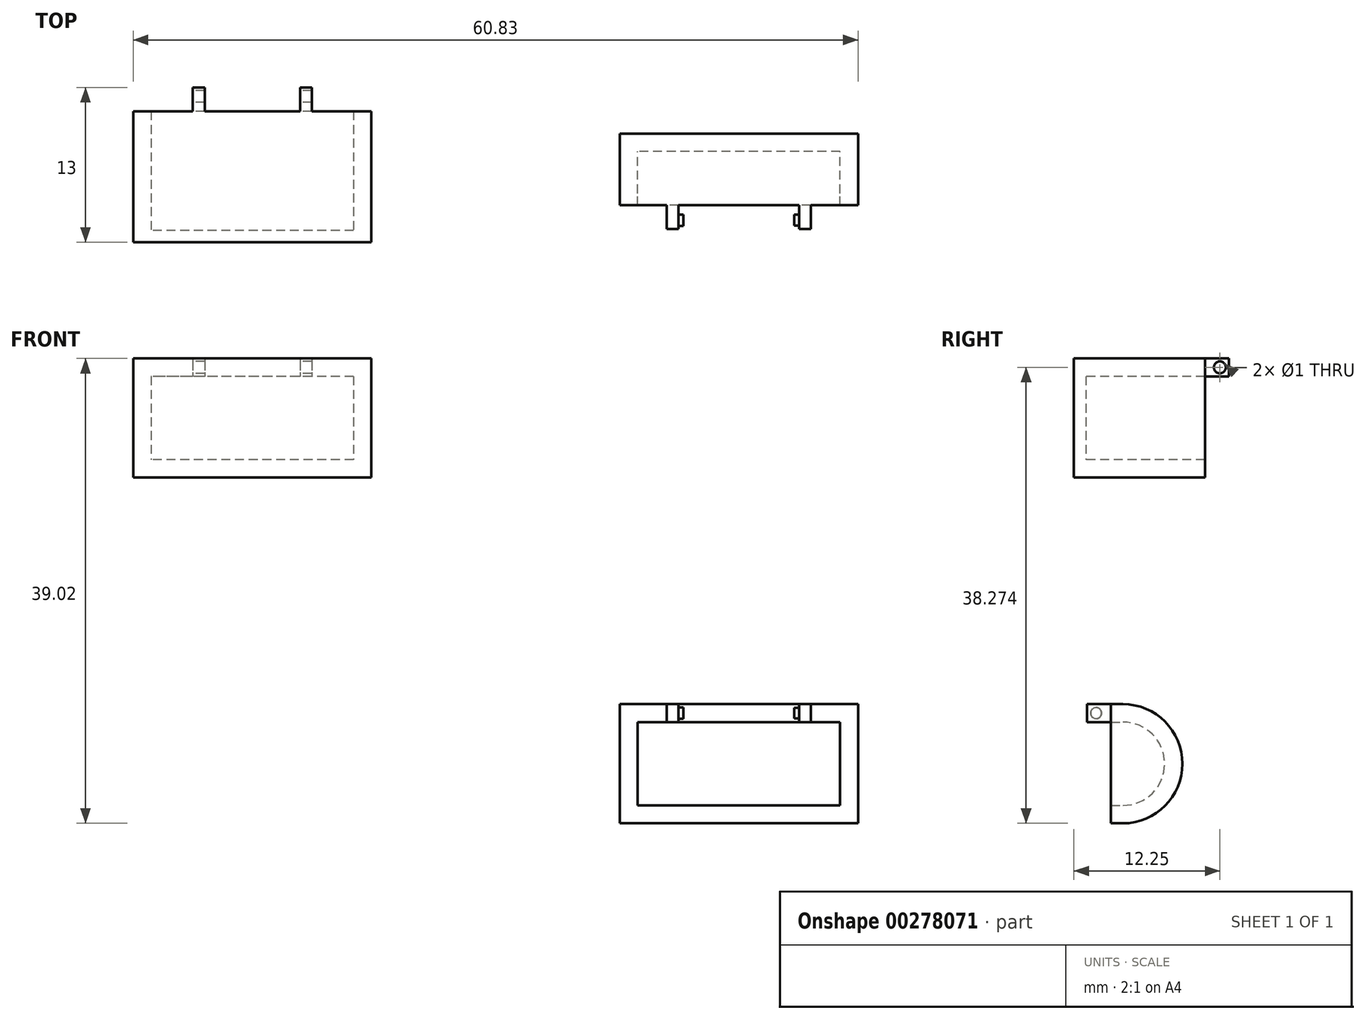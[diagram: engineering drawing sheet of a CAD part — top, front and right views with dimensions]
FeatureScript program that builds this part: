
annotation { "Feature Type Name" : "Feature", "Feature Type Description" : "" }
export const myFeature = defineFeature(function(context is Context, id is Id, definition is map)
    precondition{}
    {
        {
            var Q0;
            Q0=qCreatedBy(makeId("Front.planeOp"),FACE);
            var sketch = newSketch(context, id + "F0", { "sketchPlane" : qUnion([Q0])});
            skLineSegment(sketch, "E0.bottom", {"start": v(-40.83, 8.05) * mm, "end": v(-20.83, 8.05) * mm});
            skLineSegment(sketch, "E0.top", {"start": v(-40.83, -1.95) * mm, "end": v(-20.83, -1.95) * mm});
            skLineSegment(sketch, "E0.left", {"start": v(-40.83, 8.05) * mm, "end": v(-40.83, -1.95) * mm});
            skLineSegment(sketch, "E0.right", {"start": v(-20.83, 8.05) * mm, "end": v(-20.83, -1.95) * mm});
            skSolve(sketch);
        }
        {
            var Q0;
            Q0 = qSketchRegion(id + "F0", true);
            extrude(context, id + "F1", {"entities" : qUnion([Q0]), "oppositeDirection" : true, "depth" : 1 * mm});
        }
        {
            var Q0;
            Q0=makeQuery(id+"F1.opExtrude","CAP_FACE",FACE,{"disambiguationData":[OSD([sQuery(id+"F0.wireOp",EDGE,"E0.bottom"),sQuery(id+"F0.wireOp",EDGE,"E0.top"),sQuery(id+"F0.wireOp",EDGE,"E0.left"),sQuery(id+"F0.wireOp",EDGE,"E0.right")])],"isStart":false});
            var sketch = newSketch(context, id + "F2", { "sketchPlane" : qUnion([Q0])});
            skLineSegment(sketch, "E1.bottom", {"start": v(20.83, 8.05) * mm, "end": v(40.83, 8.05) * mm});
            skLineSegment(sketch, "E1.top", {"start": v(20.83, -1.95) * mm, "end": v(40.83, -1.95) * mm});
            skLineSegment(sketch, "E1.left", {"start": v(20.83, 8.05) * mm, "end": v(20.83, -1.95) * mm});
            skLineSegment(sketch, "E1.right", {"start": v(40.83, 8.05) * mm, "end": v(40.83, -1.95) * mm});
            skLineSegment(sketch, "E2.bottom", {"start": v(22.33, 6.55) * mm, "end": v(39.33, 6.55) * mm});
            skLineSegment(sketch, "E2.top", {"start": v(22.33, -0.45) * mm, "end": v(39.33, -0.45) * mm});
            skLineSegment(sketch, "E2.left", {"start": v(22.33, 6.55) * mm, "end": v(22.33, -0.45) * mm});
            skLineSegment(sketch, "E2.right", {"start": v(39.33, 6.55) * mm, "end": v(39.33, -0.45) * mm});
            skSolve(sketch);
        }
        {
            var Q0;
            Q0 = qSketchRegion(id + "F2", true);
            extrude(context, id + "F3", {"entities" : qUnion([Q0]), "operationType" : NewBodyOperationType.ADD, "depth" : 10 * mm});
        }
        {
            var Q0;
            Q0=makeQuery(id+"F3.opExtrude","CAP_FACE",FACE,{"disambiguationData":[OSD([sQuery(id+"F2.wireOp",EDGE,"E1.bottom"),sQuery(id+"F2.wireOp",EDGE,"E1.top"),sQuery(id+"F2.wireOp",EDGE,"E1.left"),sQuery(id+"F2.wireOp",EDGE,"E1.right"),sQuery(id+"F2.wireOp",EDGE,"E2.bottom"),sQuery(id+"F2.wireOp",EDGE,"E2.top"),sQuery(id+"F2.wireOp",EDGE,"E2.left"),sQuery(id+"F2.wireOp",EDGE,"E2.right")])],"isStart":false});
            var sketch = newSketch(context, id + "F4", { "sketchPlane" : qUnion([Q0])});
            skLineSegment(sketch, "E3.bottom", {"start": v(25.83, 8.05) * mm, "end": v(26.83, 8.05) * mm});
            skLineSegment(sketch, "E3.top", {"start": v(25.83, 6.55) * mm, "end": v(26.83, 6.55) * mm});
            skLineSegment(sketch, "E3.left", {"start": v(25.83, 8.05) * mm, "end": v(25.83, 6.55) * mm});
            skLineSegment(sketch, "E3.right", {"start": v(26.83, 8.05) * mm, "end": v(26.83, 6.55) * mm});
            skLineSegment(sketch, "E4.bottom", {"start": v(34.83, 8.05) * mm, "end": v(35.83, 8.05) * mm});
            skLineSegment(sketch, "E4.top", {"start": v(34.83, 6.55) * mm, "end": v(35.83, 6.55) * mm});
            skLineSegment(sketch, "E4.left", {"start": v(34.83, 8.05) * mm, "end": v(34.83, 6.55) * mm});
            skLineSegment(sketch, "E4.right", {"start": v(35.83, 8.05) * mm, "end": v(35.83, 6.55) * mm});
            skSolve(sketch);
        }
        {
            var Q0;
            Q0 = qSketchRegion(id + "F4", true);
            extrude(context, id + "F5", {"entities" : qUnion([Q0]), "operationType" : NewBodyOperationType.ADD, "depth" : 2 * mm});
        }
        {
            var Q0;
            Q0=makeQuery(id+"F5.opExtrude","SWEPT_FACE",FACE,{"disambiguationData":[OSD([sQuery(id+"F4.wireOp",EDGE,"E4.right")])]});
            var sketch = newSketch(context, id + "F6", { "sketchPlane" : qUnion([Q0])});
            skCircle(sketch, "E5", {"center": v(-12.25, 7.3) * mm, "radius": 0.5 * mm});
            skSolve(sketch);
        }
        {
            var Q0;
            Q0 = qSketchRegion(id + "F6", true);
            extrude(context, id + "F7", {"entities" : qUnion([Q0]), "operationType" : NewBodyOperationType.REMOVE, "oppositeDirection" : true, "depth" : 25 * mm});
        }
        {
            var Q0;
            Q0=qCreatedBy(makeId("Right.planeOp"),FACE);
            var sketch = newSketch(context, id + "F8", { "sketchPlane" : qUnion([Q0])});
            skArc(sketch, "E6", {"start": v(4.12, -30.97) * mm, "mid": v(9.12, -25.97) * mm, "end": v(4.12, -20.97) * mm});
            skLineSegment(sketch, "E7.bottom", {"start": v(4.12, -20.97) * mm, "end": v(3.12, -20.97) * mm});
            skLineSegment(sketch, "E7.top", {"start": v(4.12, -30.97) * mm, "end": v(3.12, -30.97) * mm});
            skLineSegment(sketch, "E7.right", {"start": v(3.12, -20.97) * mm, "end": v(3.12, -30.97) * mm});
            skSolve(sketch);
        }
        {
            var Q0;
            Q0 = qSketchRegion(id + "F8", true);
            extrude(context, id + "F9", {"entities" : qUnion([Q0]), "depth" : 20 * mm});
        }
        {
            var Q0;
            Q0=makeQuery(id+"F9.opExtrude","CAP_FACE",FACE,{"disambiguationData":[OSD([sQuery(id+"F8.wireOp",EDGE,"E6"),sQuery(id+"F8.wireOp",EDGE,"E7.bottom"),sQuery(id+"F8.wireOp",EDGE,"E7.top"),sQuery(id+"F8.wireOp",EDGE,"E7.right")])],"isStart":true});
            cPlane(context, id + "F10", {"entities" : qUnion([Q0]), "cplaneType" : CPlaneType.OFFSET, "offset" : 1.5 * mm, "oppositeDirection" : true, "width" : 150 * mm, "height" : 150 * mm});
        }
        {
            var Q0;
            Q0=qCreatedBy(id+"F10.planeOp",FACE);
            var sketch = newSketch(context, id + "F11", { "sketchPlane" : qUnion([Q0])});
            skArc(sketch, "E8.0", {"start": v(-4.12, -30.97) * mm, "mid": v(-9.12, -25.97) * mm, "end": v(-4.12, -20.97) * mm});
            skLineSegment(sketch, "E9.0", {"start": v(-3.12, -20.97) * mm, "end": v(-3.12, -29.47) * mm});
            skLineSegment(sketch, "E10.0", {"start": v(-4.12, -20.97) * mm, "end": v(-3.12, -20.97) * mm});
            skLineSegment(sketch, "E11.bottom", {"start": v(-3.12, -29.47) * mm, "end": v(-4.12, -29.47) * mm});
            skLineSegment(sketch, "E11.top", {"start": v(-3.12, -22.47) * mm, "end": v(-4.12, -22.47) * mm});
            skLineSegment(sketch, "E11.left", {"start": v(-3.12, -29.47) * mm, "end": v(-3.12, -22.47) * mm});
            skArc(sketch, "E12", {"start": v(-4.12, -22.47) * mm, "mid": v(-7.62, -25.97) * mm, "end": v(-4.12, -29.47) * mm});
            skPoint(sketch, "E13.orphan", {"position": v(-3.12, -30.97) * mm});
            skSolve(sketch);
        }
        {
            var Q0;
            Q0 = qSketchRegion(id + "F11", true);
            extrude(context, id + "F12", {"entities" : qUnion([Q0]), "operationType" : NewBodyOperationType.REMOVE, "oppositeDirection" : true, "depth" : (20 - 2 * 1.5) * mm});
        }
        {
            var Q0;
            Q0=makeQuery(id+"F9.opExtrude","SWEPT_FACE",FACE,{"disambiguationData":[OSD([sQuery(id+"F8.wireOp",EDGE,"E7.right")])]});
            var sketch = newSketch(context, id + "F13", { "sketchPlane" : qUnion([Q0])});
            skLineSegment(sketch, "E14.bottom", {"start": v(3.95, -20.97) * mm, "end": v(4.95, -20.97) * mm});
            skLineSegment(sketch, "E14.top", {"start": v(3.95, -22.47) * mm, "end": v(4.95, -22.47) * mm});
            skLineSegment(sketch, "E14.left", {"start": v(3.95, -20.97) * mm, "end": v(3.95, -22.47) * mm});
            skLineSegment(sketch, "E14.right", {"start": v(4.95, -20.97) * mm, "end": v(4.95, -22.47) * mm});
            skLineSegment(sketch, "E15.bottom", {"start": v(16.05, -20.97) * mm, "end": v(15.05, -20.97) * mm});
            skLineSegment(sketch, "E15.top", {"start": v(16.05, -22.47) * mm, "end": v(15.05, -22.47) * mm});
            skLineSegment(sketch, "E15.left", {"start": v(16.05, -20.97) * mm, "end": v(16.05, -22.47) * mm});
            skLineSegment(sketch, "E15.right", {"start": v(15.05, -20.97) * mm, "end": v(15.05, -22.47) * mm});
            skSolve(sketch);
        }
        {
            var Q0;
            Q0 = qSketchRegion(id + "F13", true);
            extrude(context, id + "F14", {"entities" : qUnion([Q0]), "operationType" : NewBodyOperationType.ADD, "depth" : 2 * mm});
        }
        {
            var Q0;
            Q0=makeQuery(id+"F14.opExtrude","SWEPT_FACE",FACE,{"disambiguationData":[OSD([sQuery(id+"F13.wireOp",EDGE,"E15.right")])]});
            var sketch = newSketch(context, id + "F15", { "sketchPlane" : qUnion([Q0])});
            skCircle(sketch, "E16", {"center": v(-1.87, -21.72) * mm, "radius": 0.45 * mm});
            skPoint(sketch, "E16.centerSnap0", {"position": v(-1.12, -21.72) * mm});
            skSolve(sketch);
        }
        {
            var Q0;
            Q0=makeQuery(id+"F15.imprint","IMPRINT",FACE,{"disambiguationData":[TD([[makeQuery(id+"F15.imprint","IMPRINT",EDGE,{"derivedFrom":sQuery(id+"F15.wireOp",EDGE,"E16")}),1.0]])]});
            extrude(context, id + "F16", {"entities" : qUnion([Q0]), "operationType" : NewBodyOperationType.ADD, "depth" : .4 * mm});
        }
        {
            var Q0;
            Q0=makeQuery(id+"F14.opExtrude","SWEPT_FACE",FACE,{"disambiguationData":[OSD([sQuery(id+"F13.wireOp",EDGE,"E14.right")])]});
            var sketch = newSketch(context, id + "F17", { "sketchPlane" : qUnion([Q0])});
            skCircle(sketch, "E17", {"center": v(1.87, -21.72) * mm, "radius": 0.47 * mm});
            skPoint(sketch, "E17.centerSnap0", {"position": v(1.12, -21.72) * mm});
            skSolve(sketch);
        }
        {
            var Q0;
            Q0=makeQuery(id+"F17.imprint","IMPRINT",FACE,{"disambiguationData":[TD([[makeQuery(id+"F17.imprint","IMPRINT",EDGE,{"derivedFrom":sQuery(id+"F17.wireOp",EDGE,"E17")}),1.0]])]});
            extrude(context, id + "F18", {"entities" : qUnion([Q0]), "operationType" : NewBodyOperationType.ADD, "depth" : .4 * mm});
        }
    });
